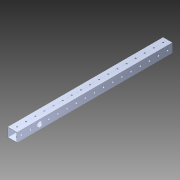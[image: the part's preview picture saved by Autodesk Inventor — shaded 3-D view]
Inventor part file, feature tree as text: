
AUTODESK INVENTOR PART (.ipt)
format: ipt  version: 2014 (Build 180170000, 170)  size: 1,278,976 bytes
history: native  units: in
note: dims shown in document units (in); Inventor stores cm internally (conversion verified against a paired STEP export)
features: sketch x3, extrude x2, pattern_circular x1, other x1, plane x1, imported_body x1
ambient origin geometry x8: Origin, YZ Plane, XZ Plane, XY Plane, X Axis, Y Axis, Z Axis, Center Point
bodies: Body1 (feature_tree)
feature tree (9):
  pattern_circular  "CirPattern2"
  other  "217-3426-STEP1"
  plane  "Work Plane1"
  extrude  "Extrusion1"  Depth=3937.0079in TaperAngle=0.0deg
  sketch  "Sketch3"  dims[d3=0.5in d5=2.0in d6=0.0in]
  extrude  "Extrusion2"  Depth=0.5in TaperAngle=0.0deg
  imported_body  "Base1"
  sketch  "Sketch1"  dims[d0=-17.0in d1=3937.0079in d2=0.0in]
  sketch  "Sketch4"
